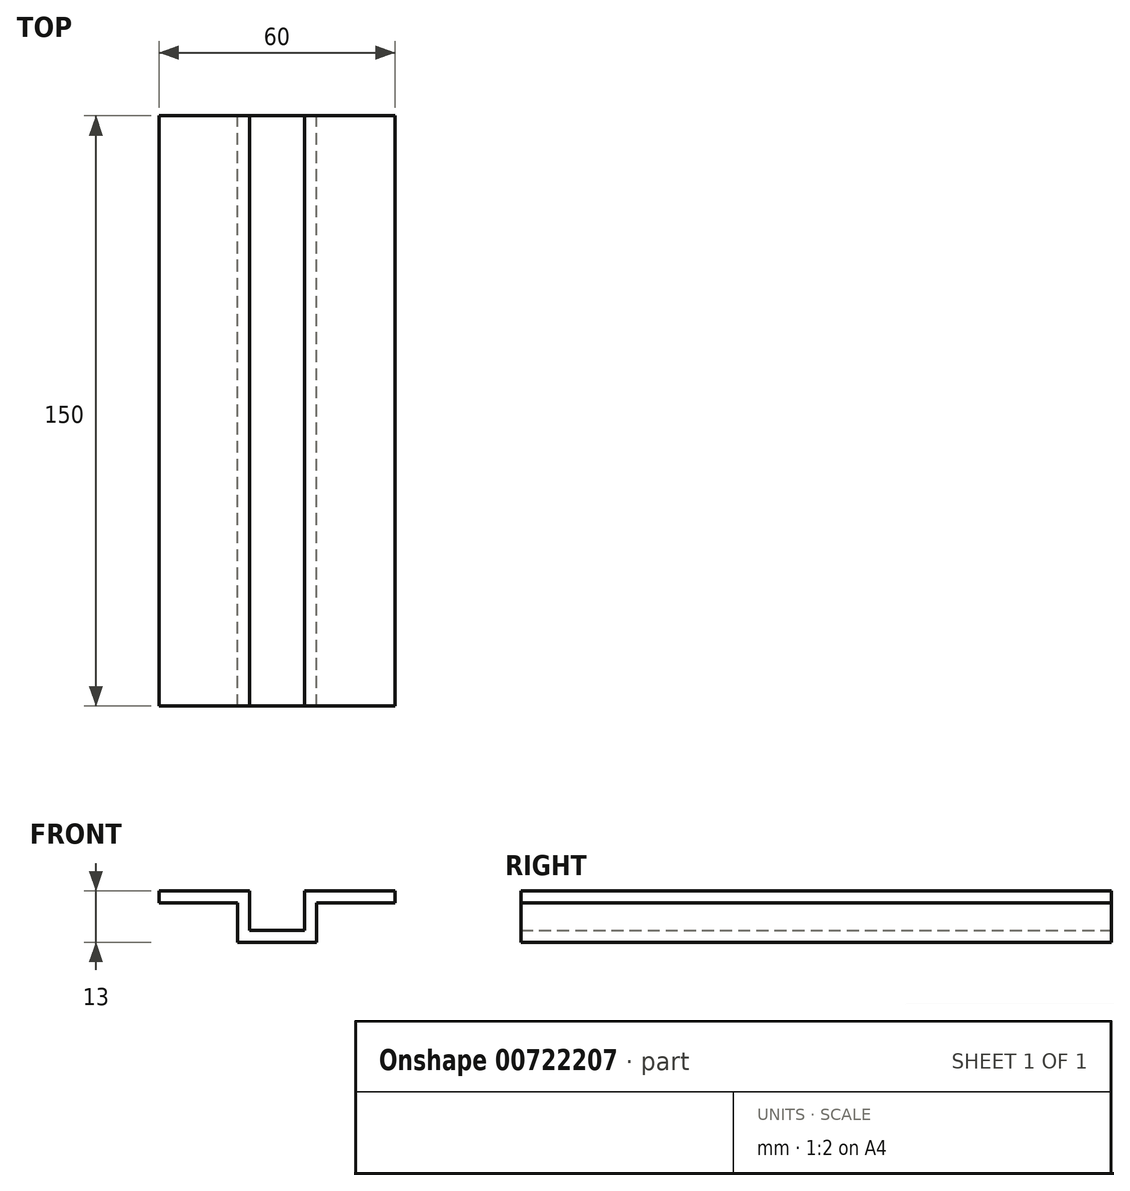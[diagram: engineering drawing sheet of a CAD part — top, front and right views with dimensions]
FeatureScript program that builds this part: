
annotation { "Feature Type Name" : "Feature", "Feature Type Description" : "" }
export const myFeature = defineFeature(function(context is Context, id is Id, definition is map)
    precondition{}
    {
        {
            var Q0;
            Q0=qCreatedBy(makeId("Front.planeOp"),FACE);
            var sketch = newSketch(context, id + "F0", { "sketchPlane" : qUnion([Q0])});
            skLineSegment(sketch, "E0", {"start": v(-56.1, 42.84) * mm, "end": v(-56.1, 39.84) * mm});
            skLineSegment(sketch, "E1", {"start": v(-56.1, 39.84) * mm, "end": v(-36.1, 39.84) * mm});
            skLineSegment(sketch, "E2", {"start": v(-56.1, 42.84) * mm, "end": v(-33.1, 42.84) * mm});
            skLineSegment(sketch, "E3", {"start": v(-36.1, 39.84) * mm, "end": v(-36.1, 29.84) * mm});
            skLineSegment(sketch, "E4", {"start": v(-33.1, 42.84) * mm, "end": v(-33.1, 32.84) * mm});
            skLineSegment(sketch, "E5", {"start": v(-36.1, 29.84) * mm, "end": v(-16.1, 29.84) * mm});
            skLineSegment(sketch, "E6", {"start": v(-33.1, 32.84) * mm, "end": v(-19.1, 32.84) * mm});
            skLineSegment(sketch, "E7", {"start": v(-16.1, 29.84) * mm, "end": v(-16.1, 39.84) * mm});
            skPoint(sketch, "E7.endSnap0", {"position": v(-46.1, 39.84) * mm});
            skLineSegment(sketch, "E8", {"start": v(-19.1, 32.84) * mm, "end": v(-19.1, 42.84) * mm});
            skLineSegment(sketch, "E9", {"start": v(-16.1, 39.84) * mm, "end": v(3.9, 39.84) * mm});
            skLineSegment(sketch, "E10", {"start": v(-19.1, 42.84) * mm, "end": v(3.9, 42.84) * mm});
            skLineSegment(sketch, "E11", {"start": v(3.9, 39.84) * mm, "end": v(3.9, 42.84) * mm});
            skSolve(sketch);
        }
        {
            var Q0;
            Q0=makeQuery(id+"F0.imprint","IMPRINT",FACE,{"disambiguationData":[TD([[makeQuery(id+"F0.imprint","IMPRINT",EDGE,{"derivedFrom":sQuery(id+"F0.wireOp",EDGE,"E0")}),1.0]])]});
            extrude(context, id + "F1", {"entities" : qUnion([Q0]), "depth" : 150 * mm, "offsetDistance" : 25 * mm});
        }
    });
